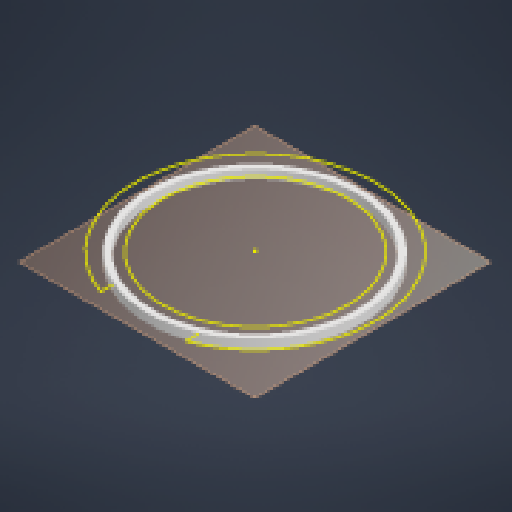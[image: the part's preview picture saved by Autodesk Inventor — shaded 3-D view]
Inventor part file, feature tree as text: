
AUTODESK INVENTOR PART (.ipt)
format: ipt  version: 2024 (Build 280153000, 153)  size: 161,280 bytes
history: native  units: mm
features: other x6, reference x5, sketch x2, extrude x2
ambient origin geometry x8: Origin, YZ Plane, XZ Plane, XY Plane, X Axis, Y Axis, Z Axis, Center Point
bodies: Body1 (feature_tree)
feature tree (15):
  other  "Твердое тело1"
  other  "РабПлоскость1"
  sketch  "Эскиз1"
  other  "РабПлоскость2"
  extrude  "Выдавливание1"  Depth=10.0mm TaperAngle=0.0deg
  extrude  "Выдавливание2"  Depth=2.0mm TaperAngle=0.0deg
  reference  "Ссылка1"
  reference  "Ссылка2"
  sketch  "Эскиз2"
  reference  "Ссылка3"
  reference  "Ссылка7"
  reference  "Ссылка8"
  parser-record x1  (decoder bookkeeping rows leaked as tree rows — omitted from the tree; the rows remain in map.json)
  other  "manipulator.iam"
  other  "platform:2"
note: 1 file-system path scrubbed to <path> (originals preserved in map.json)
